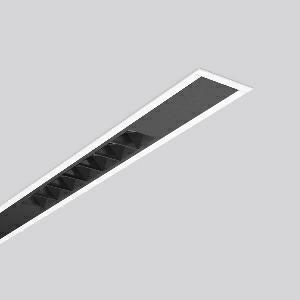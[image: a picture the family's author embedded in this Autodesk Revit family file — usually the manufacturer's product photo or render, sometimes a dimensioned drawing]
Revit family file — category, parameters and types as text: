
# Revit family: less_is_more_beamline_312478_002_eb44
name_source: partatom
category: Lighting Fixtures
units: mm (PartAtom-declared; Revit-internal decimal feet)

## family parameters
Cut with Voids When Loaded = No
Host = Face
Light Source = No
Part Type = Normal
Room Calculation Point = No
Round Connector Dimension = Use Diameter
Shared = No

## types (1)
- LESS IS MORE BEAMLINE (1 x LED Modul 930, 987.5 lm, 3000)
    Apparent Load = 47 VA
    CIE Flux Codes = 100 100 100 100 100
    Color Rendering = 90
    Color Temperature = 3000
    Default Elevation = 1800 mm
    Description = Series: LESS IS MORE BEAMLINE
Linear recessed ceiling and wall luminaire for aesthetically sophisticated lighting. Luminaire with four LED light units. Housing: extruded aluminium profile, powder-coated. End cap aluminium powder-coated. LED light unit with MRS technology: Mini-Reflector-System made of metallised thermoplastic with prismatic black glare-suppressing frame for pleasant glare-free light (RUG < 10). Each LED light unit has 7 reflector elements. Medium beam light distribution. Ceiling installation with pre-assembled SBS mounting system. LED unit with integrated converter interchangeable and removable. Suitable for through-wiring. 
Colour: traffic white, matt (RAL 9016)
Length: 2262 mm
Width: 71 mm
Height: 1.5 mm
Cut-out length: 2243 mm
Cut-out width: 60 mm
Recess height: 125 mm
Luminaire: recess height: 106 mm
Lamp: LED
Socket: without socket
Colour temperature: 3000K
Colour rendering index (CRI): 90
System power: 47 W
Rated luminous flux: 3950 lm
Luminous efficiency: 84 lm/W
Control gear: Regulated power supply
Protection class: I
Type of protection: IP 20
    Height = 0 mm  [stored 0 ft]
    Lamp = 1 x LED Modul 930
    Lamp Light Flux = 987.5 lm
    Lamp count = 1
    Length = 2262 mm
    Lifetime = 50000 h
    Luminous efficacy = 84 lm/W
    Manufacturer = RZB
    ModVariant = No
    Model = 312478.002
    Mounting Place = Ceiling, Wall
    Mounting Type = Recessed
    Number of Poles = 1
    OnlyDefault = Yes
    Power Factor = 1
    Product Name = LESS IS MORE BEAMLINE
    Product group = Recessed LED linear luminaires
    ProductGroupID = 407
    Protection Class = Protection class I
    Protection Degree = IP 20
    RLX_Detail_Level = 1
    RLX_Emergency_Light_Flux = 0 lm
    RLX_Emergency_Type = 0
    RLX_Emergency_Type_DB = No
    RlxData = <blob elided: 24325 chars, md5=94e4678e>
    Socket = socket
    Standby Power = 0 W
    System Light Flux = 3950 lm
    System Power = 47 W
    Type Comments = Product without accessories
    Type Image = 312465.002.jpg
    URL = http://relux.com
    VarID = ---
    Voltage = 230 V
    Voltage Range = 220-240 V
    Weight = 0.00 kg
    Width = 71 mm

note: [stored X ft] marks values corroborated as IEEE doubles in the binary element streams (Revit-internal decimal feet)

## geometry (parser evidence)
native form markers: Blend x4, Sweep x22
no freeform markers — native parametric forms only
